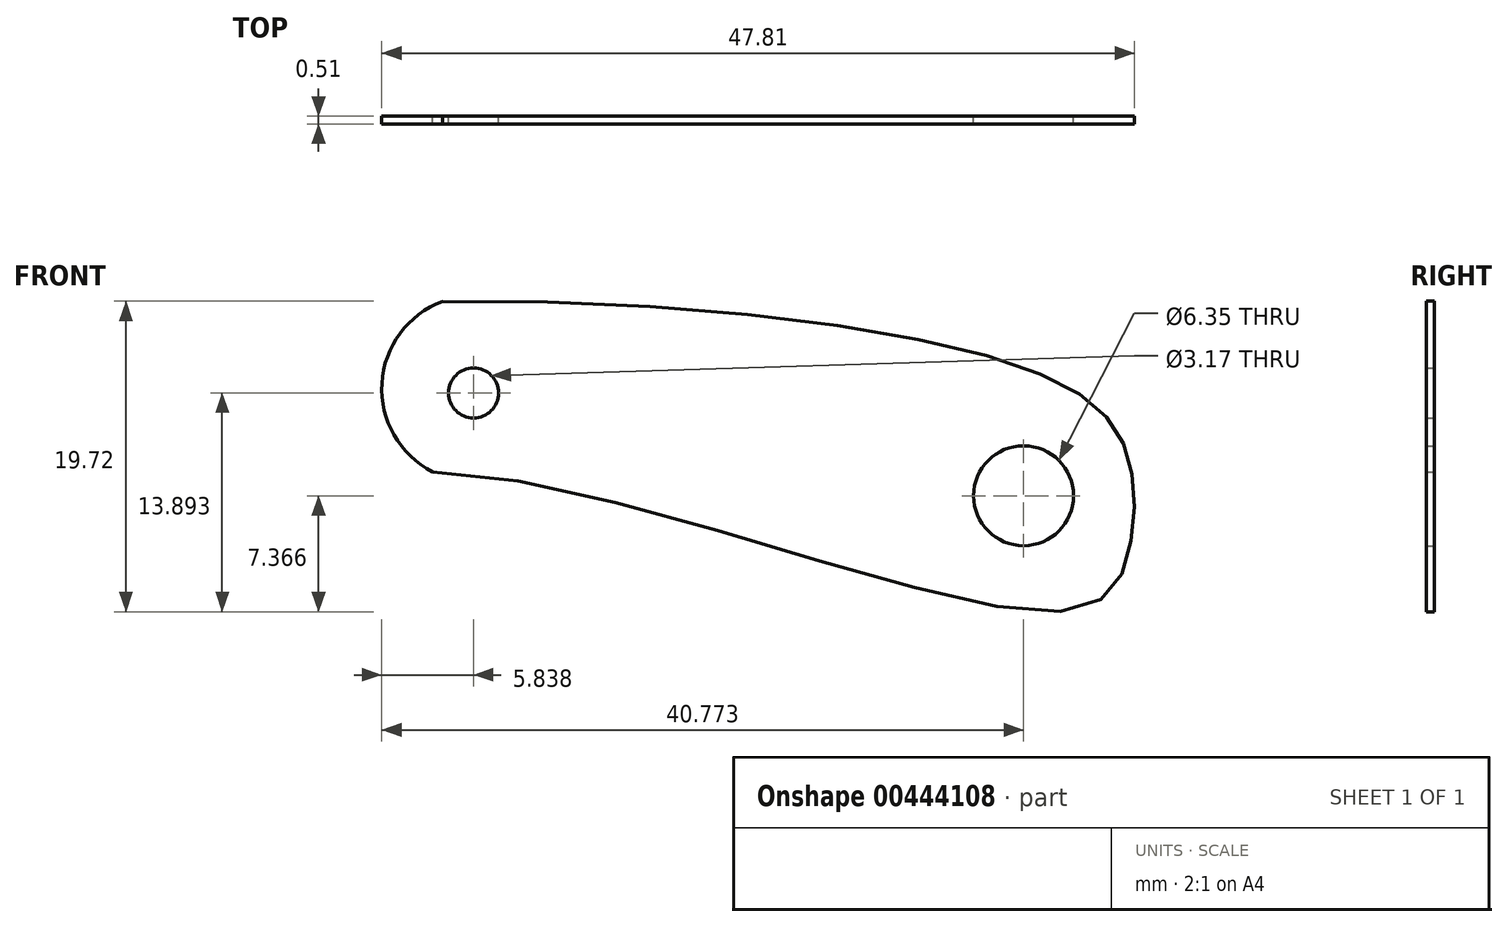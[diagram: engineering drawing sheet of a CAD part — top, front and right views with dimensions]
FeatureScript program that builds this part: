
annotation { "Feature Type Name" : "Feature", "Feature Type Description" : "" }
export const myFeature = defineFeature(function(context is Context, id is Id, definition is map)
    precondition{}
    {
        {
            var Q0;
            Q0=qCreatedBy(makeId("Front.planeOp"),FACE);
            var sketch = newSketch(context, id + "F0", { "sketchPlane" : qUnion([Q0])});
            skLineSegment(sketch, "E0", {"start": v(-1, 2.9) * mm, "end": v(0.18, 2.97) * mm});
            skPoint(sketch, "E1", {"position": v(48.62, 15.19) * mm});
            skPoint(sketch, "E2", {"position": v(13.69, 21.71) * mm});
            skArc(sketch, "E3", {"start": v(11.72, 27.52) * mm, "mid": v(7.86, 22.32) * mm, "end": v(11.07, 16.7) * mm});
            skFitSpline(sketch, "E4.trimOffspring", {"points": [v(-46.68, 0) * mm, v(-36.83, 14.74) * mm, v(0, 26.85) * mm, v(48.1, 23.51) * mm, v(54.92, 18.58) * mm, v(55.49, 12.52) * mm, v(51.4, 7.87) * mm, v(7.3, 16.37) * mm, v(0, 0) * mm], "startDerivative": vector(72.96, 165.42) * mm, "endDerivative": vector(-10.36, -190.7) * mm});
            skPoint(sketch, "E5.start.orphan", {"position": v(-1, 2.9) * mm});
            skPoint(sketch, "E6.start.orphan", {"position": v(-1.9, 17.09) * mm});
            skSolve(sketch);
        }
        {
            var Q0;
            Q0=makeQuery(id+"F0.imprint","IMPRINT",FACE,{"disambiguationData":[TD([[makeQuery(id+"F0.imprint","IMPRINT",EDGE,{"derivedFrom":sQuery(id+"F0.wireOp",EDGE,"E3")}),1.0]])]});
            extrude(context, id + "F1", {"entities" : qUnion([Q0]), "depth" : 0.5 * mm, "offsetDistance" : 25.4 * mm});
        }
        {
            var Q0;
            Q0=sQuery(id+"F0.wireOp",VERTEX,"E1");
            var Q1;
            Q1=makeQuery(id+"F1.opExtrude","SWEPT_BODY",BODY,{"disambiguationData":[OSD([sQuery(id+"F0.wireOp",EDGE,"E3"),sQuery(id+"F0.wireOp",EDGE,"E4.trimOffspring")])]});
            var Q2;
            Q2=makeQuery(id+"F1.opExtrude","SWEPT_BODY",BODY,{"disambiguationData":[OSD([sQuery(id+"F0.wireOp",EDGE,"E3"),sQuery(id+"F0.wireOp",EDGE,"E4.trimOffspring")])]});
            hole(context, id + "F2", {"style" : HoleStyle.SIMPLE, "endStyle" : HoleEndStyle.THROUGH, "oppositeDirection" : true, "holeDiameter" : 6.35 * mm, "isTappedThrough" : true, "tappedDepth" : 12.7 * mm, "tapClearance" : 3, "locations" : qUnion([Q0]), "scope" : qUnion([Q1, Q2])});
        }
        {
            var Q0;
            Q0=sQuery(id+"F0.wireOp",VERTEX,"E2");
            var Q1;
            Q1=makeQuery(id+"F1.opExtrude","SWEPT_BODY",BODY,{"disambiguationData":[OSD([sQuery(id+"F0.wireOp",EDGE,"E3"),sQuery(id+"F0.wireOp",EDGE,"E4.trimOffspring")])]});
            hole(context, id + "F3", {"style" : HoleStyle.SIMPLE, "endStyle" : HoleEndStyle.THROUGH, "oppositeDirection" : true, "holeDiameter" : 3.17 * mm, "isTappedThrough" : true, "tappedDepth" : 12.7 * mm, "tapClearance" : 3, "locations" : qUnion([Q0]), "scope" : qUnion([Q1])});
        }
    });
